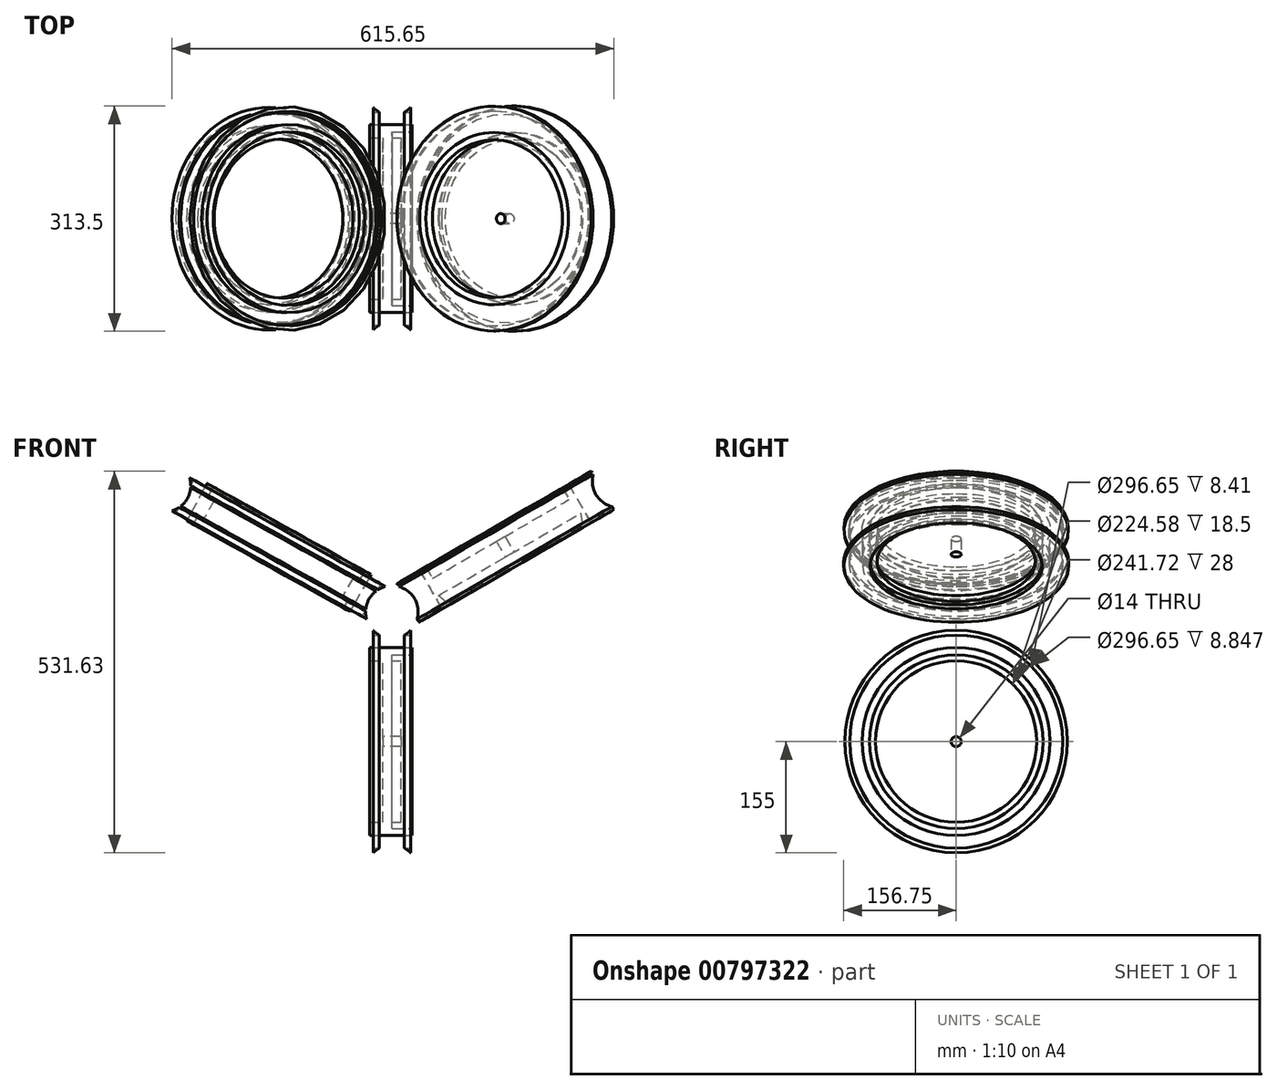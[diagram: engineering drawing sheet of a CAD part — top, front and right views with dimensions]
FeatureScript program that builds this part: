
annotation { "Feature Type Name" : "Feature", "Feature Type Description" : "" }
export const myFeature = defineFeature(function(context is Context, id is Id, definition is map)
    precondition{}
    {
        {
            var Q0;
            Q0=qCreatedBy(makeId("Front.planeOp"),FACE);
            var sketch = newSketch(context, id + "F0", { "sketchPlane" : qUnion([Q0])});
            skCircle(sketch, "E0", {"center": v(-26.84, 35.5) * mm, "radius": 36.6 * mm});
            skLineSegment(sketch, "E1", {"start": v(-26.84, 35.5) * mm, "end": v(4.86, 53.8) * mm});
            skLineSegment(sketch, "E2", {"start": v(-26.84, 35.5) * mm, "end": v(-58.53, 53.8) * mm});
            skLineSegment(sketch, "E3", {"start": v(-28.93, 37.15) * mm, "end": v(-351.93, 216.7) * mm});
            skLineSegment(sketch, "E4", {"start": v(-351.93, 216.7) * mm, "end": v(-336.87, 243.8) * mm});
            skLineSegment(sketch, "E5", {"start": v(-336.87, 243.8) * mm, "end": v(-30.49, 73.46) * mm});
            skLineSegment(sketch, "E6", {"start": v(-351.93, 216.7) * mm, "end": v(-367, 189.61) * mm});
            skLineSegment(sketch, "E7", {"start": v(-367, 189.61) * mm, "end": v(-61.48, 19.78) * mm});
            skLineSegment(sketch, "E8", {"start": v(-61.48, 19.78) * mm, "end": v(-30.49, 73.46) * mm});
            skLineSegment(sketch, "E9", {"start": v(-330.68, 246.8) * mm, "end": v(-304.7, 231.8) * mm});
            skLineSegment(sketch, "E10", {"start": v(-304.7, 231.8) * mm, "end": v(-335.7, 178.1) * mm});
            skLineSegment(sketch, "E11", {"start": v(-335.7, 178.1) * mm, "end": v(-361.68, 193.1) * mm});
            skLineSegment(sketch, "E12", {"start": v(-304.7, 231.8) * mm, "end": v(-296.04, 226.8) * mm});
            skLineSegment(sketch, "E13", {"start": v(-296.04, 226.8) * mm, "end": v(-297.54, 224.2) * mm});
            skLineSegment(sketch, "E14", {"start": v(-297.54, 224.2) * mm, "end": v(-306.2, 229.2) * mm});
            skLineSegment(sketch, "E15", {"start": v(-335.7, 178.1) * mm, "end": v(-327.04, 173.1) * mm});
            skLineSegment(sketch, "E16", {"start": v(-327.04, 173.1) * mm, "end": v(-325.54, 175.7) * mm});
            skLineSegment(sketch, "E17", {"start": v(-325.54, 175.7) * mm, "end": v(-334.2, 180.7) * mm});
            skLineSegment(sketch, "E18", {"start": v(-297.54, 224.2) * mm, "end": v(-325.54, 175.7) * mm});
            skLineSegment(sketch, "E19", {"start": v(-60.73, 18.6) * mm, "end": v(-95.37, 38.6) * mm});
            skLineSegment(sketch, "E20", {"start": v(-95.37, 38.6) * mm, "end": v(-64.37, 92.3) * mm});
            skLineSegment(sketch, "E21", {"start": v(-183.68, 158.63) * mm, "end": v(-214.23, 104.7) * mm});
            skLineSegment(sketch, "E22", {"start": v(-24.13, 36.88) * mm, "end": v(295.43, 221.38) * mm});
            skLineSegment(sketch, "E23", {"start": v(295.43, 221.38) * mm, "end": v(310.93, 194.54) * mm});
            skLineSegment(sketch, "E24", {"start": v(295.43, 221.38) * mm, "end": v(279.93, 248.23) * mm});
            skLineSegment(sketch, "E25", {"start": v(279.93, 248.23) * mm, "end": v(-22.79, 73.46) * mm});
            skLineSegment(sketch, "E26", {"start": v(8.22, 19.77) * mm, "end": v(310.93, 194.54) * mm});
            skLineSegment(sketch, "E27", {"start": v(126.09, 159.4) * mm, "end": v(157.09, 105.72) * mm});
            skLineSegment(sketch, "E28", {"start": v(277.44, 246.8) * mm, "end": v(251.46, 231.8) * mm});
            skLineSegment(sketch, "E29", {"start": v(253.95, 233.23) * mm, "end": v(284.95, 179.54) * mm});
            skLineSegment(sketch, "E30", {"start": v(282.46, 178.1) * mm, "end": v(273.8, 173.1) * mm});
            skLineSegment(sketch, "E31", {"start": v(273.8, 173.1) * mm, "end": v(272.3, 175.7) * mm});
            skLineSegment(sketch, "E32", {"start": v(274.8, 177.14) * mm, "end": v(283.45, 182.14) * mm});
            skLineSegment(sketch, "E33", {"start": v(251.46, 231.8) * mm, "end": v(242.8, 226.8) * mm});
            skLineSegment(sketch, "E34", {"start": v(242.8, 226.8) * mm, "end": v(244.3, 224.2) * mm});
            skLineSegment(sketch, "E35", {"start": v(246.8, 225.63) * mm, "end": v(255.45, 230.63) * mm});
            skLineSegment(sketch, "E36", {"start": v(246.8, 225.63) * mm, "end": v(274.8, 177.14) * mm});
            skLineSegment(sketch, "E37", {"start": v(8.22, 19.77) * mm, "end": v(37.87, 36.89) * mm});
            skLineSegment(sketch, "E38", {"start": v(-25.27, 72.02) * mm, "end": v(9.37, 92.02) * mm});
            skLineSegment(sketch, "E39", {"start": v(11.86, 93.46) * mm, "end": v(42.86, 39.77) * mm});
            skLineSegment(sketch, "E40", {"start": v(9.37, 92.02) * mm, "end": v(0.71, 87.02) * mm});
            skLineSegment(sketch, "E41", {"start": v(3.2, 88.46) * mm, "end": v(4.7, 85.86) * mm});
            skLineSegment(sketch, "E42", {"start": v(4.7, 85.86) * mm, "end": v(13.36, 90.86) * mm});
            skLineSegment(sketch, "E43", {"start": v(40.37, 38.33) * mm, "end": v(31.71, 33.33) * mm});
            skLineSegment(sketch, "E44", {"start": v(49.4, 47.62) * mm, "end": v(47.9, 50.22) * mm});
            skLineSegment(sketch, "E45", {"start": v(39.6, 45.43) * mm, "end": v(47.9, 50.22) * mm});
            skLineSegment(sketch, "E46", {"start": v(-26.62, 32.75) * mm, "end": v(-26.62, -336.25) * mm});
            skLineSegment(sketch, "E47", {"start": v(-26.62, -336.25) * mm, "end": v(4.38, -336.25) * mm});
            skLineSegment(sketch, "E48", {"start": v(4.38, -336.25) * mm, "end": v(4.38, 13.3) * mm});
            skLineSegment(sketch, "E49", {"start": v(4.38, 13.3) * mm, "end": v(-57.62, 13.3) * mm});
            skLineSegment(sketch, "E50", {"start": v(-57.62, 13.3) * mm, "end": v(-57.62, -336.25) * mm});
            skLineSegment(sketch, "E51", {"start": v(-57.62, -336.25) * mm, "end": v(-26.62, -336.25) * mm});
            skLineSegment(sketch, "E52", {"start": v(-57.62, 13.3) * mm, "end": v(-57.62, -26.7) * mm});
            skLineSegment(sketch, "E53", {"start": v(-57.62, -24.17) * mm, "end": v(4.38, -24.17) * mm});
            skLineSegment(sketch, "E54", {"start": v(4.38, -24.17) * mm, "end": v(1.38, -24.17) * mm});
            skLineSegment(sketch, "E55", {"start": v(1.38, -24.17) * mm, "end": v(1.38, -14.17) * mm});
            skLineSegment(sketch, "E56", {"start": v(1.38, -14.17) * mm, "end": v(4.38, -14.17) * mm});
            skLineSegment(sketch, "E57", {"start": v(-57.62, -22.74) * mm, "end": v(-57.62, -12.74) * mm});
            skLineSegment(sketch, "E58", {"start": v(-57.62, -333.55) * mm, "end": v(-57.62, -293.55) * mm});
            skLineSegment(sketch, "E59", {"start": v(-57.62, -293.55) * mm, "end": v(4.38, -293.55) * mm});
            skLineSegment(sketch, "E60", {"start": v(4.38, -293.55) * mm, "end": v(4.38, -24.17) * mm});
            skLineSegment(sketch, "E61", {"start": v(4.38, -161.48) * mm, "end": v(-57.62, -161.48) * mm});
            skLineSegment(sketch, "E62", {"start": v(-57.62, -293.55) * mm, "end": v(-57.62, -303.55) * mm});
            skLineSegment(sketch, "E63", {"start": v(-57.62, -303.55) * mm, "end": v(-54.62, -303.55) * mm});
            skLineSegment(sketch, "E64", {"start": v(-54.62, -303.55) * mm, "end": v(-54.62, -293.55) * mm});
            skLineSegment(sketch, "E65", {"start": v(4.38, -293.55) * mm, "end": v(4.38, -303.55) * mm});
            skLineSegment(sketch, "E66", {"start": v(4.38, -303.55) * mm, "end": v(1.38, -303.55) * mm});
            skLineSegment(sketch, "E67", {"start": v(-64.37, 92.3) * mm, "end": v(-55.71, 87.3) * mm});
            skLineSegment(sketch, "E68", {"start": v(-55.71, 87.3) * mm, "end": v(-57.21, 84.7) * mm});
            skLineSegment(sketch, "E69", {"start": v(-57.21, 84.7) * mm, "end": v(-65.87, 89.7) * mm});
            skLineSegment(sketch, "E70", {"start": v(-95.37, 38.6) * mm, "end": v(-93.87, 41.2) * mm});
            skLineSegment(sketch, "E71", {"start": v(-93.87, 41.2) * mm, "end": v(-85.21, 36.2) * mm});
            skLineSegment(sketch, "E72", {"start": v(-85.21, 36.2) * mm, "end": v(-86.4, 34.16) * mm});
            skLineSegment(sketch, "E73", {"start": v(-57.62, 16) * mm, "end": v(-55.62, 16) * mm});
            skLineSegment(sketch, "E74", {"start": v(-55.62, 13.3) * mm, "end": v(-55.62, 3.3) * mm});
            skLineSegment(sketch, "E75", {"start": v(-55.62, 3.3) * mm, "end": v(2.38, 3.3) * mm});
            skLineSegment(sketch, "E76", {"start": v(2.38, 3.3) * mm, "end": v(2.38, 13.3) * mm});
            skLineSegment(sketch, "E77", {"start": v(-27.97, 72.02) * mm, "end": v(-28.97, 70.3) * mm});
            skLineSegment(sketch, "E78", {"start": v(-31.67, 71.85) * mm, "end": v(-40.41, 76.7) * mm});
            skLineSegment(sketch, "E79", {"start": v(-40.41, 76.7) * mm, "end": v(-69.41, 26.48) * mm});
            skLineSegment(sketch, "E80", {"start": v(-69.41, 26.48) * mm, "end": v(-60.48, 21.51) * mm});
            skLineSegment(sketch, "E81", {"start": v(-57.97, 20.06) * mm, "end": v(-58.97, 18.33) * mm});
            skLineSegment(sketch, "E82", {"start": v(5.51, 18.39) * mm, "end": v(4.51, 20.12) * mm});
            skLineSegment(sketch, "E83", {"start": v(7.22, 21.5) * mm, "end": v(15.88, 26.5) * mm});
            skLineSegment(sketch, "E84", {"start": v(15.88, 26.5) * mm, "end": v(-13.12, 76.73) * mm});
            skLineSegment(sketch, "E85", {"start": v(-13.12, 76.73) * mm, "end": v(-21.74, 71.75) * mm});
            skLineSegment(sketch, "E86", {"start": v(-22.79, 73.46) * mm, "end": v(-21.74, 71.75) * mm});
            skLineSegment(sketch, "E87", {"start": v(8.22, 19.77) * mm, "end": v(7.22, 21.5) * mm});
            skLineSegment(sketch, "E88", {"start": v(-61.48, 19.78) * mm, "end": v(-57.62, 13.3) * mm});
            skLineSegment(sketch, "E89", {"start": v(-30.49, 73.46) * mm, "end": v(-22.79, 73.46) * mm});
            skLineSegment(sketch, "E90", {"start": v(8.22, 19.77) * mm, "end": v(4.38, 13.3) * mm});
            skLineSegment(sketch, "E91", {"start": v(-86.4, 34.16) * mm, "end": v(-55.71, 87.3) * mm});
            skLineSegment(sketch, "E92", {"start": v(-69.41, 26.48) * mm, "end": v(-67.91, 29.08) * mm});
            skLineSegment(sketch, "E93", {"start": v(-67.91, 29.08) * mm, "end": v(-62.15, 25.87) * mm});
            skLineSegment(sketch, "E94", {"start": v(-62.15, 25.87) * mm, "end": v(-64.65, 21.54) * mm});
            skLineSegment(sketch, "E95", {"start": v(-40.41, 76.7) * mm, "end": v(-41.91, 74.1) * mm});
            skLineSegment(sketch, "E96", {"start": v(-41.91, 74.1) * mm, "end": v(-36.3, 70.86) * mm});
            skLineSegment(sketch, "E97", {"start": v(-36.3, 70.86) * mm, "end": v(-33.82, 75.31) * mm});
            skLineSegment(sketch, "E98", {"start": v(-64.65, 21.54) * mm, "end": v(-200.12, 96.85) * mm});
            skLineSegment(sketch, "E99", {"start": v(-200.12, 96.85) * mm, "end": v(-170, 151.03) * mm});
            skLineSegment(sketch, "E100", {"start": v(-185.06, 123.94) * mm, "end": v(-176.79, 138.82) * mm});
            skLineSegment(sketch, "E101", {"start": v(-185.06, 123.94) * mm, "end": v(-192.1, 111.27) * mm});
            skLineSegment(sketch, "E102", {"start": v(-200.12, 96.85) * mm, "end": v(-192.1, 111.27) * mm});
            skLineSegment(sketch, "E103", {"start": v(-170, 151.03) * mm, "end": v(-176.79, 138.82) * mm});
            skLineSegment(sketch, "E104", {"start": v(-176.79, 138.82) * mm, "end": v(-48.7, 64.87) * mm});
            skLineSegment(sketch, "E105", {"start": v(-192.1, 111.27) * mm, "end": v(-63.2, 39.62) * mm});
            skLineSegment(sketch, "E106", {"start": v(-64.37, 92.3) * mm, "end": v(-73.11, 97.16) * mm});
            skLineSegment(sketch, "E107", {"start": v(-73.11, 97.16) * mm, "end": v(-103.23, 42.99) * mm});
            skLineSegment(sketch, "E108", {"start": v(47.9, 50.22) * mm, "end": v(4.7, 85.86) * mm});
            skLineSegment(sketch, "E109", {"start": v(14.38, 29.1) * mm, "end": v(8.41, 25.65) * mm});
            skLineSegment(sketch, "E110", {"start": v(-13.12, 76.73) * mm, "end": v(-11.62, 74.13) * mm});
            skLineSegment(sketch, "E111", {"start": v(-11.62, 74.13) * mm, "end": v(-17.31, 70.85) * mm});
            skLineSegment(sketch, "E112", {"start": v(-17.31, 70.85) * mm, "end": v(-19.81, 75.18) * mm});
            skLineSegment(sketch, "E113", {"start": v(12.42, 22.2) * mm, "end": v(146.66, 99.7) * mm});
            skLineSegment(sketch, "E114", {"start": v(146.66, 99.7) * mm, "end": v(115.66, 153.39) * mm});
            skLineSegment(sketch, "E115", {"start": v(115.66, 153.39) * mm, "end": v(124.9, 137.37) * mm});
            skLineSegment(sketch, "E116", {"start": v(124.9, 137.37) * mm, "end": v(-3.17, 63.42) * mm});
            skLineSegment(sketch, "E117", {"start": v(124.9, 137.37) * mm, "end": v(137.4, 115.72) * mm});
            skLineSegment(sketch, "E118", {"start": v(137.4, 115.72) * mm, "end": v(9.23, 41.71) * mm});
            skLineSegment(sketch, "E119", {"start": v(42.86, 39.77) * mm, "end": v(51.52, 44.77) * mm});
            skLineSegment(sketch, "E120", {"start": v(51.52, 44.77) * mm, "end": v(20.52, 98.46) * mm});
            skLineSegment(sketch, "E121", {"start": v(2.38, 3.3) * mm, "end": v(-0.62, 3.3) * mm});
            skLineSegment(sketch, "E122", {"start": v(-0.62, 3.3) * mm, "end": v(-0.62, 9.97) * mm});
            skLineSegment(sketch, "E123", {"start": v(-0.62, 9.97) * mm, "end": v(4.38, 9.97) * mm});
            skLineSegment(sketch, "E124", {"start": v(-55.62, 3.3) * mm, "end": v(-52.62, 3.3) * mm});
            skLineSegment(sketch, "E125", {"start": v(-52.62, 3.3) * mm, "end": v(-52.62, 9.53) * mm});
            skLineSegment(sketch, "E126", {"start": v(-52.62, 9.53) * mm, "end": v(-57.62, 9.53) * mm});
            skLineSegment(sketch, "E127", {"start": v(-57.62, 9.53) * mm, "end": v(-57.62, -24.17) * mm});
            skLineSegment(sketch, "E128", {"start": v(-57.62, -22.74) * mm, "end": v(-57.62, -32.74) * mm});
            skLineSegment(sketch, "E129", {"start": v(-57.62, -32.74) * mm, "end": v(4.38, -32.74) * mm});
            skLineSegment(sketch, "E130", {"start": v(4.38, 9.97) * mm, "end": v(4.38, -145.03) * mm});
            skLineSegment(sketch, "E131", {"start": v(4.38, -145.03) * mm, "end": v(-57.62, -145.03) * mm});
            skLineSegment(sketch, "E132", {"start": v(-57.62, -145.03) * mm, "end": v(-39.12, -145.03) * mm});
            skLineSegment(sketch, "E133", {"start": v(-39.12, -145.03) * mm, "end": v(-39.12, -32.74) * mm});
            skLineSegment(sketch, "E134", {"start": v(-39.12, -32.74) * mm, "end": v(-14.12, -32.74) * mm});
            skLineSegment(sketch, "E135", {"start": v(-14.12, -32.74) * mm, "end": v(-14.12, -145.03) * mm});
            skLineSegment(sketch, "E136", {"start": v(1.38, -14.17) * mm, "end": v(-57.62, -14.17) * mm});
            skLineSegment(sketch, "E137", {"start": v(-21.74, 71.75) * mm, "end": v(7.22, 21.5) * mm});
            skLineSegment(sketch, "E138", {"start": v(8.41, 25.65) * mm, "end": v(10.91, 21.32) * mm});
            skLineSegment(sketch, "E139", {"start": v(12.42, 22.2) * mm, "end": v(10.91, 21.32) * mm});
            skSolve(sketch);
        }
        {
            var Q0;
            {var subQ6=sQuery(id+"F0.wireOp",EDGE,"E70");Q0=makeQuery(id+"F0.imprint","IMPRINT",FACE,{"disambiguationData":[TD([[makeQuery(id+"F0.imprint","IMPRINT",EDGE,{"derivedFrom":subQ6}),1.0]])]});}
            var Q1;
            {var subQ0=sQuery(id+"F0.wireOp",EDGE,"E71");Q1=makeQuery(id+"F0.imprint","IMPRINT",FACE,{"disambiguationData":[TD([[makeQuery(id+"F0.imprint","IMPRINT",EDGE,{"derivedFrom":subQ0}),1.0]])]});}
            var Q2;
            {var subQ0=sQuery(id+"F0.wireOp",EDGE,"E91");var subQ1=sQuery(id+"F0.wireOp",EDGE,"E3");var subQ2=makeQuery(id+"F0.imprint","INTERSECT",VERTEX,{"derivedFrom":[subQ1,subQ0]});Q2=makeQuery(id+"F0.imprint","IMPRINT",FACE,{"disambiguationData":[TD([[makeQuery(id+"F0.imprint","IMPRINT",EDGE,{"disambiguationData":[TD([[subQ2,-1.0]])],"derivedFrom":subQ1}),1.0]])]});}
            var Q3;
            {var subQ0=sQuery(id+"F0.wireOp",EDGE,"E20");var subQ1=sQuery(id+"F0.wireOp",EDGE,"E3");var subQ2=makeQuery(id+"F0.imprint","INTERSECT",VERTEX,{"derivedFrom":[subQ1,subQ0]});Q3=makeQuery(id+"F0.imprint","IMPRINT",FACE,{"disambiguationData":[TD([[makeQuery(id+"F0.imprint","IMPRINT",EDGE,{"disambiguationData":[TD([[subQ2,-1.0]])],"derivedFrom":subQ1}),1.0]])]});}
            var Q4;
            {var subQ0=sQuery(id+"F0.wireOp",EDGE,"E20");var subQ1=sQuery(id+"F0.wireOp",EDGE,"E3");var subQ2=makeQuery(id+"F0.imprint","INTERSECT",VERTEX,{"derivedFrom":[subQ1,subQ0]});Q4=makeQuery(id+"F0.imprint","IMPRINT",FACE,{"disambiguationData":[TD([[makeQuery(id+"F0.imprint","IMPRINT",EDGE,{"disambiguationData":[TD([[subQ2,-1.0]])],"derivedFrom":subQ1}),-1.0]])]});}
            var Q5;
            {var subQ0=sQuery(id+"F0.wireOp",EDGE,"E91");var subQ1=sQuery(id+"F0.wireOp",EDGE,"E3");var subQ2=makeQuery(id+"F0.imprint","INTERSECT",VERTEX,{"derivedFrom":[subQ1,subQ0]});Q5=makeQuery(id+"F0.imprint","IMPRINT",FACE,{"disambiguationData":[TD([[makeQuery(id+"F0.imprint","IMPRINT",EDGE,{"disambiguationData":[TD([[subQ2,-1.0]])],"derivedFrom":subQ1}),-1.0]])]});}
            var Q6;
            {var subQ0=sQuery(id+"F0.wireOp",EDGE,"E69");Q6=makeQuery(id+"F0.imprint","IMPRINT",FACE,{"disambiguationData":[TD([[makeQuery(id+"F0.imprint","IMPRINT",EDGE,{"derivedFrom":subQ0}),1.0]])]});}
            var Q7;
            {var subQ0=sQuery(id+"F0.wireOp",EDGE,"E106");Q7=makeQuery(id+"F0.imprint","IMPRINT",FACE,{"disambiguationData":[TD([[makeQuery(id+"F0.imprint","IMPRINT",EDGE,{"derivedFrom":subQ0}),1.0]])]});}
            var Q8;
            {var subQ0=sQuery(id+"F0.wireOp",EDGE,"E67");Q8=makeQuery(id+"F0.imprint","IMPRINT",FACE,{"disambiguationData":[TD([[makeQuery(id+"F0.imprint","IMPRINT",EDGE,{"derivedFrom":subQ0}),-1.0]])]});}
            var Q9;
            {var subQ0=sQuery(id+"F0.wireOp",EDGE,"E100");Q9=makeQuery(id+"F0.imprint","IMPRINT",FACE,{"disambiguationData":[TD([[makeQuery(id+"F0.imprint","IMPRINT",EDGE,{"derivedFrom":subQ0}),-1.0]])]});}
            var Q10;
            {var subQ0=sQuery(id+"F0.wireOp",EDGE,"E101");Q10=makeQuery(id+"F0.imprint","IMPRINT",FACE,{"disambiguationData":[TD([[makeQuery(id+"F0.imprint","IMPRINT",EDGE,{"derivedFrom":subQ0}),1.0]])]});}
            var Q11;
            Q11=sQuery(id+"F0.wireOp",EDGE,"E100");
            revolve(context, id + "F1", {"surfaceOperationType" : NewSurfaceOperationType.NEW, "entities" : qUnion([Q0, Q1, Q2, Q3, Q4, Q5, Q6, Q7, Q8, Q9, Q10]), "axis" : qUnion([Q11]), "revolveType" : RevolveType.FULL});
        }
        {
            var Q0;
            {var subQ0=sQuery(id+"F0.wireOp",EDGE,"E95");Q0=makeQuery(id+"F0.imprint","IMPRINT",FACE,{"disambiguationData":[TD([[makeQuery(id+"F0.imprint","IMPRINT",EDGE,{"derivedFrom":subQ0}),-1.0]])]});}
            var Q1;
            {var subQ0=sQuery(id+"F0.wireOp",EDGE,"E104");var subQ1=sQuery(id+"F0.wireOp",EDGE,"E0");var subQ2=makeQuery(id+"F0.imprint","INTERSECT",VERTEX,{"derivedFrom":[subQ1,subQ0]});Q1=makeQuery(id+"F0.imprint","IMPRINT",FACE,{"disambiguationData":[TD([[makeQuery(id+"F0.imprint","IMPRINT",EDGE,{"disambiguationData":[TD([[subQ2,-1.0]])],"derivedFrom":subQ1}),-1.0]])]});}
            var Q2;
            {var subQ0=sQuery(id+"F0.wireOp",EDGE,"E105");var subQ1=sQuery(id+"F0.wireOp",EDGE,"E0");var subQ2=makeQuery(id+"F0.imprint","INTERSECT",VERTEX,{"derivedFrom":[subQ1,subQ0]});Q2=makeQuery(id+"F0.imprint","IMPRINT",FACE,{"disambiguationData":[TD([[makeQuery(id+"F0.imprint","IMPRINT",EDGE,{"disambiguationData":[TD([[subQ2,1.0]])],"derivedFrom":subQ1}),-1.0]])]});}
            var Q3;
            {var subQ0=sQuery(id+"F0.wireOp",EDGE,"E92");Q3=makeQuery(id+"F0.imprint","IMPRINT",FACE,{"disambiguationData":[TD([[makeQuery(id+"F0.imprint","IMPRINT",EDGE,{"derivedFrom":subQ0}),1.0]])]});}
            var Q4;
            {var subQ0=sQuery(id+"F0.wireOp",EDGE,"E92");Q4=makeQuery(id+"F0.imprint","IMPRINT",FACE,{"disambiguationData":[TD([[makeQuery(id+"F0.imprint","IMPRINT",EDGE,{"derivedFrom":subQ0}),-1.0]])]});}
            var Q5;
            {var subQ0=sQuery(id+"F0.wireOp",EDGE,"E93");Q5=makeQuery(id+"F0.imprint","IMPRINT",FACE,{"disambiguationData":[TD([[makeQuery(id+"F0.imprint","IMPRINT",EDGE,{"derivedFrom":subQ0}),1.0]])]});}
            var Q6;
            {var subQ0=sQuery(id+"F0.wireOp",EDGE,"E96");Q6=makeQuery(id+"F0.imprint","IMPRINT",FACE,{"disambiguationData":[TD([[makeQuery(id+"F0.imprint","IMPRINT",EDGE,{"derivedFrom":subQ0}),-1.0]])]});}
            var Q7;
            {var subQ0=sQuery(id+"F0.wireOp",EDGE,"E95");Q7=makeQuery(id+"F0.imprint","IMPRINT",FACE,{"disambiguationData":[TD([[makeQuery(id+"F0.imprint","IMPRINT",EDGE,{"derivedFrom":subQ0}),1.0]])]});}
            var Q8;
            Q8=makeQuery(id+"F1.opRevolve","SWEPT_FACE",FACE,{"disambiguationData":[OSD([sQuery(id+"F0.wireOp",EDGE,"E91")])]});
            revolve(context, id + "F2", {"surfaceOperationType" : NewSurfaceOperationType.NEW, "entities" : qUnion([Q0, Q1, Q2, Q3, Q4, Q5, Q6, Q7]), "axis" : qUnion([Q8]), "revolveType" : RevolveType.FULL});
        }
        {
            var Q0;
            {var subQ0=sQuery(id+"F0.wireOp",EDGE,"E120");var subQ1=sQuery(id+"F0.wireOp",EDGE,"E22");var subQ2=makeQuery(id+"F0.imprint","INTERSECT",VERTEX,{"derivedFrom":[subQ1,subQ0]});Q0=makeQuery(id+"F0.imprint","IMPRINT",FACE,{"disambiguationData":[TD([[makeQuery(id+"F0.imprint","IMPRINT",EDGE,{"disambiguationData":[TD([[subQ2,-1.0]])],"derivedFrom":subQ1}),-1.0]])]});}
            var Q1;
            {var subQ0=sQuery(id+"F0.wireOp",EDGE,"E120");var subQ1=sQuery(id+"F0.wireOp",EDGE,"E22");var subQ2=makeQuery(id+"F0.imprint","INTERSECT",VERTEX,{"derivedFrom":[subQ1,subQ0]});Q1=makeQuery(id+"F0.imprint","IMPRINT",FACE,{"disambiguationData":[TD([[makeQuery(id+"F0.imprint","IMPRINT",EDGE,{"disambiguationData":[TD([[subQ2,-1.0]])],"derivedFrom":subQ1}),1.0]])]});}
            var Q2;
            {var subQ1=sQuery(id+"F0.wireOp",EDGE,"E39");var subQ6=sQuery(id+"F0.wireOp",EDGE,"E25");var subQ8=makeQuery(id+"F0.imprint","INTERSECT",VERTEX,{"derivedFrom":[subQ6,subQ1]});Q2=makeQuery(id+"F0.imprint","IMPRINT",FACE,{"disambiguationData":[TD([[makeQuery(id+"F0.imprint","IMPRINT",EDGE,{"disambiguationData":[TD([[subQ8,1.0]])],"derivedFrom":subQ6}),1.0]])]});}
            var Q3;
            {var subQ0=sQuery(id+"F0.wireOp",EDGE,"E39");var subQ1=sQuery(id+"F0.wireOp",EDGE,"E22");var subQ2=makeQuery(id+"F0.imprint","INTERSECT",VERTEX,{"derivedFrom":[subQ1,subQ0]});Q3=makeQuery(id+"F0.imprint","IMPRINT",FACE,{"disambiguationData":[TD([[makeQuery(id+"F0.imprint","IMPRINT",EDGE,{"disambiguationData":[TD([[subQ2,-1.0]])],"derivedFrom":subQ1}),1.0]])]});}
            var Q4;
            {var subQ0=sQuery(id+"F0.wireOp",EDGE,"E108");var subQ1=sQuery(id+"F0.wireOp",EDGE,"E22");var subQ2=makeQuery(id+"F0.imprint","INTERSECT",VERTEX,{"derivedFrom":[subQ1,subQ0]});Q4=makeQuery(id+"F0.imprint","IMPRINT",FACE,{"disambiguationData":[TD([[makeQuery(id+"F0.imprint","IMPRINT",EDGE,{"disambiguationData":[TD([[subQ2,-1.0]])],"derivedFrom":subQ1}),1.0]])]});}
            var Q5;
            {var subQ0=sQuery(id+"F0.wireOp",EDGE,"E108");var subQ1=sQuery(id+"F0.wireOp",EDGE,"E22");var subQ2=makeQuery(id+"F0.imprint","INTERSECT",VERTEX,{"derivedFrom":[subQ1,subQ0]});Q5=makeQuery(id+"F0.imprint","IMPRINT",FACE,{"disambiguationData":[TD([[makeQuery(id+"F0.imprint","IMPRINT",EDGE,{"disambiguationData":[TD([[subQ2,-1.0]])],"derivedFrom":subQ1}),-1.0]])]});}
            var Q6;
            {var subQ0=sQuery(id+"F0.wireOp",EDGE,"E39");var subQ1=sQuery(id+"F0.wireOp",EDGE,"E22");var subQ2=makeQuery(id+"F0.imprint","INTERSECT",VERTEX,{"derivedFrom":[subQ1,subQ0]});Q6=makeQuery(id+"F0.imprint","IMPRINT",FACE,{"disambiguationData":[TD([[makeQuery(id+"F0.imprint","IMPRINT",EDGE,{"disambiguationData":[TD([[subQ2,-1.0]])],"derivedFrom":subQ1}),-1.0]])]});}
            var Q7;
            {var subQ0=sQuery(id+"F0.wireOp",EDGE,"E119");Q7=makeQuery(id+"F0.imprint","IMPRINT",FACE,{"disambiguationData":[TD([[makeQuery(id+"F0.imprint","IMPRINT",EDGE,{"derivedFrom":subQ0}),1.0]])]});}
            var Q8;
            {var subQ4=sQuery(id+"F0.wireOp",EDGE,"E44");Q8=makeQuery(id+"F0.imprint","IMPRINT",FACE,{"disambiguationData":[TD([[makeQuery(id+"F0.imprint","IMPRINT",EDGE,{"derivedFrom":subQ4}),-1.0]])]});}
            var Q9;
            {var subQ0=sQuery(id+"F0.wireOp",EDGE,"E45");Q9=makeQuery(id+"F0.imprint","IMPRINT",FACE,{"disambiguationData":[TD([[makeQuery(id+"F0.imprint","IMPRINT",EDGE,{"derivedFrom":subQ0}),1.0]])]});}
            var Q10;
            Q10=sQuery(id+"F0.wireOp",EDGE,"E114");
            revolve(context, id + "F3", {"surfaceOperationType" : NewSurfaceOperationType.NEW, "entities" : qUnion([Q0, Q1, Q2, Q3, Q4, Q5, Q6, Q7, Q8, Q9]), "axis" : qUnion([Q10]), "revolveType" : RevolveType.FULL});
        }
        {
            var Q0;
            {var subQ0=sQuery(id+"F0.wireOp",EDGE,"E118");var subQ1=sQuery(id+"F0.wireOp",EDGE,"E0");var subQ2=makeQuery(id+"F0.imprint","INTERSECT",VERTEX,{"derivedFrom":[subQ1,subQ0]});Q0=makeQuery(id+"F0.imprint","IMPRINT",FACE,{"disambiguationData":[TD([[makeQuery(id+"F0.imprint","IMPRINT",EDGE,{"disambiguationData":[TD([[subQ2,-1.0]])],"derivedFrom":subQ1}),-1.0]])]});}
            var Q1;
            {var subQ1=sQuery(id+"F0.wireOp",EDGE,"E0");var subQ5=makeQuery(id+"F0.imprint","INTERSECT",VERTEX,{"derivedFrom":[subQ1,sQuery(id+"F0.wireOp",EDGE,"E1")]});Q1=makeQuery(id+"F0.imprint","IMPRINT",FACE,{"disambiguationData":[TD([[makeQuery(id+"F0.imprint","IMPRINT",EDGE,{"disambiguationData":[TD([[subQ5,1.0]])],"derivedFrom":subQ1}),-1.0]])]});}
            var Q2;
            {var subQ3=sQuery(id+"F0.wireOp",EDGE,"E41");Q2=makeQuery(id+"F0.imprint","IMPRINT",FACE,{"disambiguationData":[TD([[makeQuery(id+"F0.imprint","IMPRINT",EDGE,{"derivedFrom":subQ3}),-1.0]])]});}
            var Q3;
            {var subQ0=sQuery(id+"F0.wireOp",EDGE,"E42");Q3=makeQuery(id+"F0.imprint","IMPRINT",FACE,{"disambiguationData":[TD([[makeQuery(id+"F0.imprint","IMPRINT",EDGE,{"derivedFrom":subQ0}),-1.0]])]});}
            var Q4;
            {var subQ0=sQuery(id+"F0.wireOp",EDGE,"E41");Q4=makeQuery(id+"F0.imprint","IMPRINT",FACE,{"disambiguationData":[TD([[makeQuery(id+"F0.imprint","IMPRINT",EDGE,{"derivedFrom":subQ0}),1.0]])]});}
            var Q5;
            {var subQ0=sQuery(id+"F0.wireOp",EDGE,"E116");var subQ1=sQuery(id+"F0.wireOp",EDGE,"E39");var subQ2=makeQuery(id+"F0.imprint","INTERSECT",VERTEX,{"derivedFrom":[subQ1,subQ0]});Q5=makeQuery(id+"F0.imprint","IMPRINT",FACE,{"disambiguationData":[TD([[makeQuery(id+"F0.imprint","IMPRINT",EDGE,{"disambiguationData":[TD([[subQ2,-1.0]])],"derivedFrom":subQ1}),-1.0]])]});}
            var Q6;
            {var subQ0=sQuery(id+"F0.wireOp",EDGE,"E111");Q6=makeQuery(id+"F0.imprint","IMPRINT",FACE,{"disambiguationData":[TD([[makeQuery(id+"F0.imprint","IMPRINT",EDGE,{"derivedFrom":subQ0}),1.0]])]});}
            var Q7;
            {var subQ0=sQuery(id+"F0.wireOp",EDGE,"E110");Q7=makeQuery(id+"F0.imprint","IMPRINT",FACE,{"disambiguationData":[TD([[makeQuery(id+"F0.imprint","IMPRINT",EDGE,{"derivedFrom":subQ0}),-1.0]])]});}
            var Q8;
            {var subQ5=sQuery(id+"F0.wireOp",EDGE,"E109");Q8=makeQuery(id+"F0.imprint","IMPRINT",FACE,{"disambiguationData":[TD([[makeQuery(id+"F0.imprint","IMPRINT",EDGE,{"derivedFrom":subQ5}),1.0]])]});}
            var Q9;
            {var subQ0=sQuery(id+"F0.wireOp",EDGE,"E109");Q9=makeQuery(id+"F0.imprint","IMPRINT",FACE,{"disambiguationData":[TD([[makeQuery(id+"F0.imprint","IMPRINT",EDGE,{"derivedFrom":subQ0}),-1.0]])]});}
            var Q10;
            {var subQ5=sQuery(id+"F0.wireOp",EDGE,"E139");Q10=makeQuery(id+"F0.imprint","IMPRINT",FACE,{"disambiguationData":[TD([[makeQuery(id+"F0.imprint","IMPRINT",EDGE,{"derivedFrom":subQ5}),-1.0]])]});}
            var Q11;
            Q11=sQuery(id+"F0.wireOp",EDGE,"E114");
            revolve(context, id + "F4", {"surfaceOperationType" : NewSurfaceOperationType.NEW, "entities" : qUnion([Q0, Q1, Q2, Q3, Q4, Q5, Q6, Q7, Q8, Q9, Q10]), "axis" : qUnion([Q11]), "revolveType" : RevolveType.FULL});
        }
        {
            var Q0;
            {var subQ0=sQuery(id+"F0.wireOp",EDGE,"E54");Q0=makeQuery(id+"F0.imprint","IMPRINT",FACE,{"disambiguationData":[TD([[makeQuery(id+"F0.imprint","IMPRINT",EDGE,{"derivedFrom":subQ0}),-1.0]])]});}
            var Q1;
            {var subQ5=sQuery(id+"F0.wireOp",EDGE,"E55");Q1=makeQuery(id+"F0.imprint","IMPRINT",FACE,{"disambiguationData":[TD([[makeQuery(id+"F0.imprint","IMPRINT",EDGE,{"derivedFrom":subQ5}),1.0]])]});}
            var Q2;
            {var subQ5=sQuery(id+"F0.wireOp",EDGE,"E46");var subQ7=sQuery(id+"F0.wireOp",EDGE,"E136");var subQ9=makeQuery(id+"F0.imprint","INTERSECT",VERTEX,{"derivedFrom":[subQ5,subQ7]});Q2=makeQuery(id+"F0.imprint","IMPRINT",FACE,{"disambiguationData":[TD([[makeQuery(id+"F0.imprint","IMPRINT",EDGE,{"disambiguationData":[TD([[subQ9,-1.0]])],"derivedFrom":subQ5}),-1.0]])]});}
            var Q3;
            {var subQ5=sQuery(id+"F0.wireOp",EDGE,"E53");var subQ7=sQuery(id+"F0.wireOp",EDGE,"E46");var subQ8=makeQuery(id+"F0.imprint","INTERSECT",VERTEX,{"derivedFrom":[subQ7,subQ5]});Q3=makeQuery(id+"F0.imprint","IMPRINT",FACE,{"disambiguationData":[TD([[makeQuery(id+"F0.imprint","IMPRINT",EDGE,{"disambiguationData":[TD([[subQ8,-1.0]])],"derivedFrom":subQ7}),-1.0]])]});}
            var Q4;
            {var subQ5=sQuery(id+"F0.wireOp",EDGE,"E54");Q4=makeQuery(id+"F0.imprint","IMPRINT",FACE,{"disambiguationData":[TD([[makeQuery(id+"F0.imprint","IMPRINT",EDGE,{"derivedFrom":subQ5}),1.0]])]});}
            var Q5;
            {var subQ5=sQuery(id+"F0.wireOp",EDGE,"E135");Q5=makeQuery(id+"F0.imprint","IMPRINT",FACE,{"disambiguationData":[TD([[makeQuery(id+"F0.imprint","IMPRINT",EDGE,{"derivedFrom":subQ5}),-1.0]])]});}
            var Q6;
            {var subQ5=sQuery(id+"F0.wireOp",EDGE,"E133");Q6=makeQuery(id+"F0.imprint","IMPRINT",FACE,{"disambiguationData":[TD([[makeQuery(id+"F0.imprint","IMPRINT",EDGE,{"derivedFrom":subQ5}),-1.0]])]});}
            var Q7;
            Q7=sQuery(id+"F0.wireOp",EDGE,"E131");
            revolve(context, id + "F5", {"surfaceOperationType" : NewSurfaceOperationType.NEW, "entities" : qUnion([Q0, Q1, Q2, Q3, Q4, Q5, Q6]), "axis" : qUnion([Q7]), "revolveType" : RevolveType.FULL});
        }
        {
            var Q0;
            {var subQ4=sQuery(id+"F0.wireOp",EDGE,"E56");Q0=makeQuery(id+"F0.imprint","IMPRINT",FACE,{"disambiguationData":[TD([[makeQuery(id+"F0.imprint","IMPRINT",EDGE,{"derivedFrom":subQ4}),1.0]])]});}
            var Q1;
            {var subQ0=sQuery(id+"F0.wireOp",EDGE,"E121");Q1=makeQuery(id+"F0.imprint","IMPRINT",FACE,{"disambiguationData":[TD([[makeQuery(id+"F0.imprint","IMPRINT",EDGE,{"derivedFrom":subQ0}),-1.0]])]});}
            var Q2;
            {var subQ0=sQuery(id+"F0.wireOp",EDGE,"E122");Q2=makeQuery(id+"F0.imprint","IMPRINT",FACE,{"disambiguationData":[TD([[makeQuery(id+"F0.imprint","IMPRINT",EDGE,{"derivedFrom":subQ0}),1.0]])]});}
            var Q3;
            {var subQ0=sQuery(id+"F0.wireOp",EDGE,"E125");Q3=makeQuery(id+"F0.imprint","IMPRINT",FACE,{"disambiguationData":[TD([[makeQuery(id+"F0.imprint","IMPRINT",EDGE,{"derivedFrom":subQ0}),-1.0]])]});}
            var Q4;
            {var subQ0=sQuery(id+"F0.wireOp",EDGE,"E124");Q4=makeQuery(id+"F0.imprint","IMPRINT",FACE,{"disambiguationData":[TD([[makeQuery(id+"F0.imprint","IMPRINT",EDGE,{"derivedFrom":subQ0}),1.0]])]});}
            var Q5;
            {var subQ0=sQuery(id+"F0.wireOp",EDGE,"E124");Q5=makeQuery(id+"F0.imprint","IMPRINT",FACE,{"disambiguationData":[TD([[makeQuery(id+"F0.imprint","IMPRINT",EDGE,{"derivedFrom":subQ0}),-1.0]])]});}
            var Q6;
            Q6=sQuery(id+"F0.wireOp",EDGE,"E131");
            revolve(context, id + "F6", {"surfaceOperationType" : NewSurfaceOperationType.NEW, "entities" : qUnion([Q0, Q1, Q2, Q3, Q4, Q5]), "axis" : qUnion([Q6]), "revolveType" : RevolveType.FULL});
        }
        {
            var Q0;
            Q0=makeQuery(id+"F3.opRevolve","SWEPT_FACE",FACE,{"disambiguationData":[OSD([sQuery(id+"F0.wireOp",EDGE,"E118")])]});
            var sketch = newSketch(context, id + "F7", { "sketchPlane" : qUnion([Q0])});
            skCircle(sketch, "E140", {"center": v(176.86, 0) * mm, "radius": 7 * mm});
            skSolve(sketch);
        }
        {
            var Q0;
            Q0 = qSketchRegion(id + "F7", true);
            extrude(context, id + "F8", {"entities" : qUnion([Q0]), "operationType" : NewBodyOperationType.REMOVE, "endBound" : BoundingType.THROUGH_ALL, "oppositeDirection" : true, "depth" : 25 * mm, "offsetDistance" : 25 * mm});
        }
        {
            var Q0;
            Q0=makeQuery(id+"F5.opRevolve","SWEPT_FACE",FACE,{"disambiguationData":[OSD([sQuery(id+"F0.wireOp",EDGE,"E133")])]});
            var sketch = newSketch(context, id + "F9", { "sketchPlane" : qUnion([Q0])});
            skCircle(sketch, "E141", {"center": v(0, -145.03) * mm, "radius": 7 * mm});
            skSolve(sketch);
        }
        {
            var Q0;
            Q0 = qSketchRegion(id + "F9", true);
            extrude(context, id + "F10", {"entities" : qUnion([Q0]), "operationType" : NewBodyOperationType.REMOVE, "endBound" : BoundingType.THROUGH_ALL, "oppositeDirection" : true, "depth" : 25 * mm, "offsetDistance" : 25 * mm});
        }
        {
            var Q0;
            Q0=makeQuery(id+"F1.opRevolve","SWEPT_FACE",FACE,{"disambiguationData":[OSD([sQuery(id+"F0.wireOp",EDGE,"E105")])]});
            var sketch = newSketch(context, id + "F11", { "sketchPlane" : qUnion([Q0])});
            skLineSegment(sketch, "E142", {"start": v(-223.17, 110.85) * mm, "end": v(-223.17, -110.85) * mm});
            skCircle(sketch, "E143", {"center": v(-223.17, 0) * mm, "radius": 7 * mm});
            skSolve(sketch);
        }
        {
            var Q0;
            Q0 = qSketchRegion(id + "F11", true);
            extrude(context, id + "F12", {"entities" : qUnion([Q0]), "operationType" : NewBodyOperationType.REMOVE, "endBound" : BoundingType.THROUGH_ALL, "oppositeDirection" : true, "depth" : 25 * mm, "offsetDistance" : 25 * mm});
        }
    });
